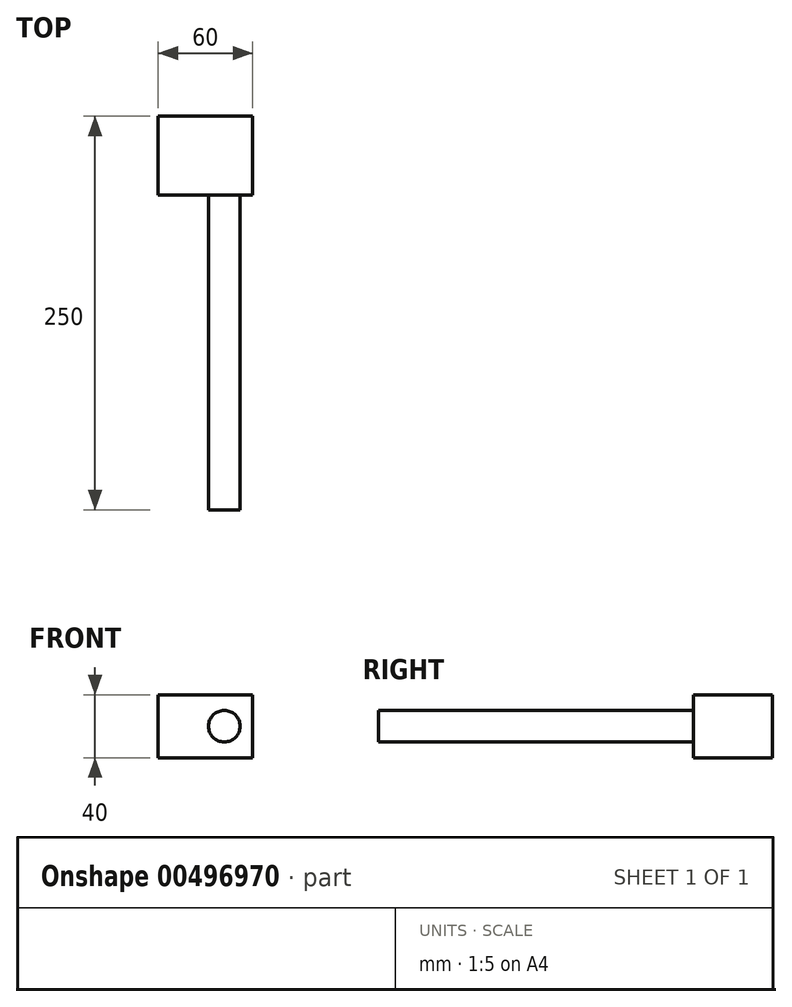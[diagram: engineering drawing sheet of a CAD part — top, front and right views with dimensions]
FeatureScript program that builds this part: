
annotation { "Feature Type Name" : "Feature", "Feature Type Description" : "" }
export const myFeature = defineFeature(function(context is Context, id is Id, definition is map)
    precondition{}
    {
        {
            var Q0;
            Q0=qCreatedBy(makeId("Front.planeOp"),FACE);
            var sketch = newSketch(context, id + "F0", { "sketchPlane" : qUnion([Q0])});
            skLineSegment(sketch, "E0.bottom", {"start": v(30, -20) * mm, "end": v(-30, -20) * mm});
            skLineSegment(sketch, "E0.top", {"start": v(30, 20) * mm, "end": v(-30, 20) * mm});
            skLineSegment(sketch, "E0.left", {"start": v(30, -20) * mm, "end": v(30, 20) * mm});
            skLineSegment(sketch, "E0.right", {"start": v(-30, -20) * mm, "end": v(-30, 20) * mm});
            skPoint(sketch, "E0.middle", {"position": v(0, 0) * mm});
            skSolve(sketch);
        }
        {
            var Q0;
            Q0=qSketchRegion(id+"F0",true);
            extrude(context, id + "F1", {"entities" : qUnion([Q0]), "depth" : 50 * mm});
        }
        {
            var Q0;
            Q0=makeQuery(id+"F1.opExtrude","CAP_FACE",FACE,{"disambiguationData":[OSD([sQuery(id+"F0.wireOp",EDGE,"E0.bottom"),sQuery(id+"F0.wireOp",EDGE,"E0.top"),sQuery(id+"F0.wireOp",EDGE,"E0.left"),sQuery(id+"F0.wireOp",EDGE,"E0.right")])],"isStart":false});
            var sketch = newSketch(context, id + "F2", { "sketchPlane" : qUnion([Q0])});
            skCircle(sketch, "E1", {"center": v(12, 0) * mm, "radius": 10 * mm});
            skSolve(sketch);
        }
        {
            var Q0;
            Q0=qSketchRegion(id+"F2",true);
            extrude(context, id + "F3", {"entities" : qUnion([Q0]), "depth" : 200 * mm});
        }
    });
